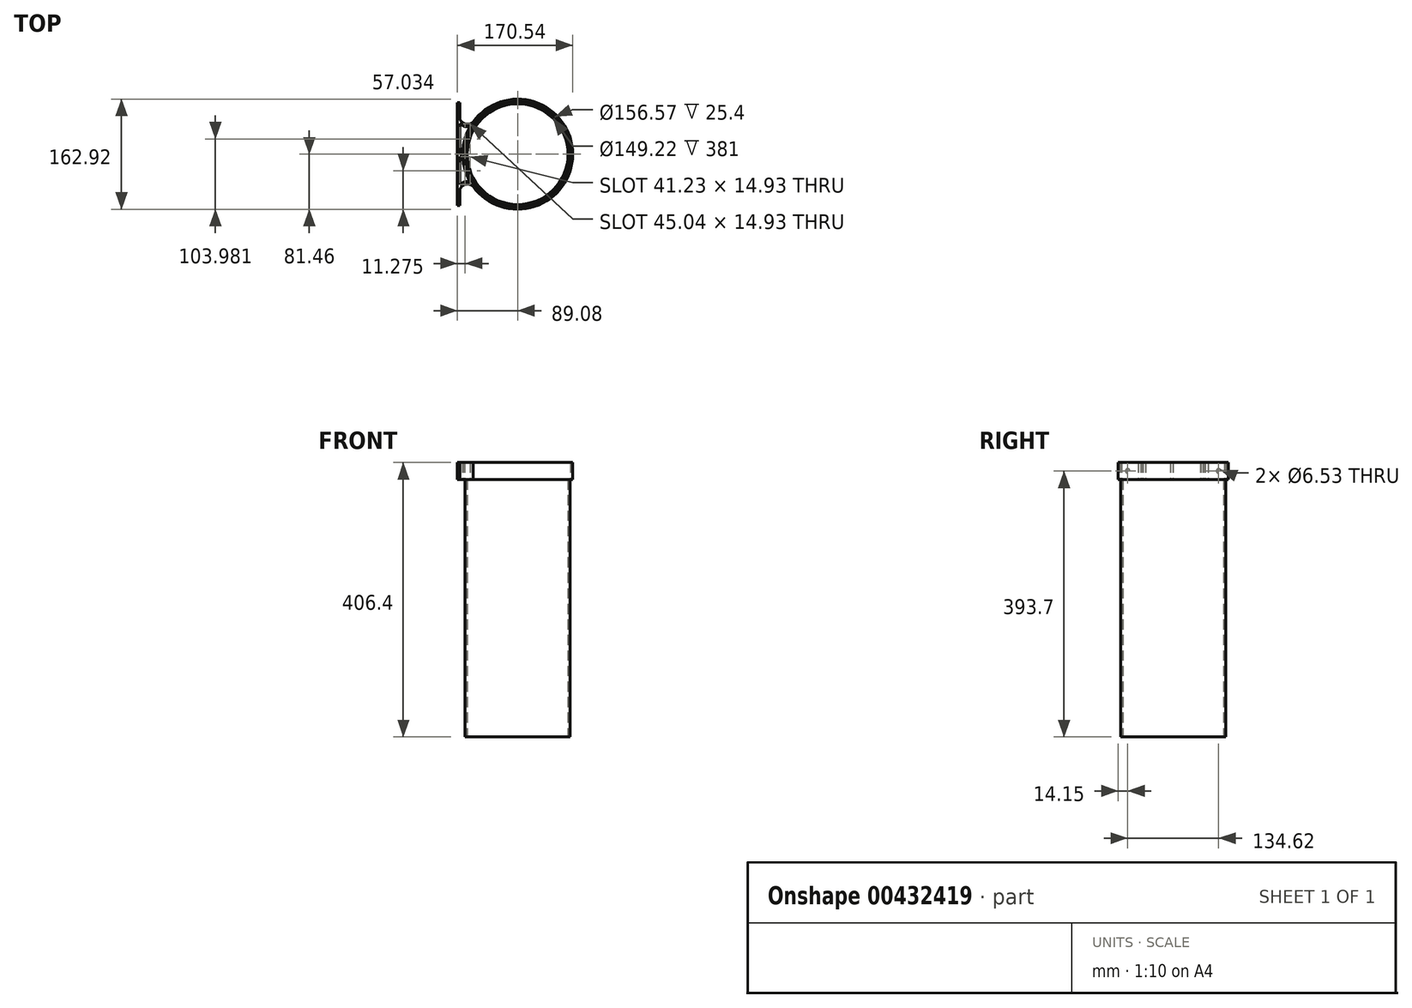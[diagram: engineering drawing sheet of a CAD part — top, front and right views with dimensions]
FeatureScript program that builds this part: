
annotation { "Feature Type Name" : "Feature", "Feature Type Description" : "" }
export const myFeature = defineFeature(function(context is Context, id is Id, definition is map)
    precondition{}
    {
        {
            var Q0;
            Q0=qCreatedBy(makeId("Top.planeOp"),FACE);
            var sketch = newSketch(context, id + "F0", { "sketchPlane" : qUnion([Q0])});
            skCircle(sketch, "E0", {"center": v(0, 0) * mm, "radius": 77.79 * mm});
            skCircle(sketch, "E1.0", {"center": v(0, 0) * mm, "radius": 74.61 * mm});
            skSolve(sketch);
        }
        {
            var Q0;
            Q0 = qSketchRegion(id + "F0", true);
            extrude(context, id + "F1", {"entities" : qUnion([Q0]), "depth" : 381 * mm});
        }
        {
            var Q0;
            Q0=makeQuery(id+"F1.opExtrude","CAP_FACE",FACE,{"disambiguationData":[OSD([sQuery(id+"F0.wireOp",EDGE,"E0"),sQuery(id+"F0.wireOp",EDGE,"E1.0")])],"isStart":false});
            var sketch = newSketch(context, id + "F2", { "sketchPlane" : qUnion([Q0])});
            skCircle(sketch, "E2", {"center": v(0, 0) * mm, "radius": 78.29 * mm});
            skLineSegment(sketch, "E3", {"start": v(77.79, 0) * mm, "end": v(78.29, 0) * mm});
            skArc(sketch, "E4.0", {"start": v(-70.34, 41.1) * mm, "mid": v(68.26, -44.46) * mm, "end": v(-66.02, 47.72) * mm});
            skLineSegment(sketch, "E5", {"start": v(-81.46, 0) * mm, "end": v(-89.08, 0) * mm});
            skLineSegment(sketch, "E6", {"start": v(-89.08, 0) * mm, "end": v(-89.08, 76.2) * mm});
            skLineSegment(sketch, "E7.0", {"start": v(-85.27, 0) * mm, "end": v(-85.27, 45.04) * mm});
            skArc(sketch, "E8", {"start": v(-85.27, 51.62) * mm, "mid": v(-76.67, 44.64) * mm, "end": v(-66.02, 47.72) * mm});
            skArc(sketch, "E9.0", {"start": v(-85.27, 45.04) * mm, "mid": v(-78.32, 41.11) * mm, "end": v(-70.34, 41.1) * mm});
            skLineSegment(sketch, "E10.trimOffspring", {"start": v(-85.27, 51.62) * mm, "end": v(-85.27, 76.2) * mm});
            skLineSegment(sketch, "E11", {"start": v(-89.08, 76.2) * mm, "end": v(-85.27, 76.2) * mm});
            skLineSegment(sketch, "E12.MirrorCS", {"start": v(-89.08, -76.2) * mm, "end": v(-85.27, -76.2) * mm});
            skArc(sketch, "E13.MirrorCS", {"start": v(-85.27, -51.62) * mm, "mid": v(-76.67, -44.64) * mm, "end": v(-66.02, -47.72) * mm});
            skLineSegment(sketch, "E14.MirrorCS", {"start": v(-85.27, 0) * mm, "end": v(-85.27, -45.04) * mm});
            skLineSegment(sketch, "E15.MirrorCS", {"start": v(-89.08, 0) * mm, "end": v(-89.08, -76.2) * mm});
            skArc(sketch, "E16.MirrorCS", {"start": v(-85.27, -45.04) * mm, "mid": v(-78.32, -41.11) * mm, "end": v(-70.34, -41.1) * mm});
            skLineSegment(sketch, "E17.MirrorCS", {"start": v(-85.27, -51.62) * mm, "end": v(-85.27, -76.2) * mm});
            skLineSegment(sketch, "E18", {"start": v(-85.27, 0) * mm, "end": v(-85.27, 3.81) * mm});
            skLineSegment(sketch, "E19", {"start": v(-85.27, 3.81) * mm, "end": v(-81.37, 3.81) * mm});
            skLineSegment(sketch, "E20.MirrorCS", {"start": v(-85.27, -3.81) * mm, "end": v(-81.37, -3.81) * mm});
            skSolve(sketch);
        }
        {
            var Q0;
            Q0 = qSketchRegion(id + "F2", true);
            var Q1;
            {var subQ4=sQuery(id+"F2.wireOp",EDGE,"E18");Q1=makeQuery(id+"F2.imprint","IMPRINT",FACE,{"disambiguationData":[TD([[makeQuery(id+"F2.imprint","IMPRINT",EDGE,{"derivedFrom":subQ4}),-1.0]])]});}
            var Q2;
            {var subQ3=sQuery(id+"F2.wireOp",EDGE,"E20.MirrorCS");Q2=makeQuery(id+"F2.imprint","IMPRINT",FACE,{"disambiguationData":[TD([[makeQuery(id+"F2.imprint","IMPRINT",EDGE,{"derivedFrom":subQ3}),1.0]])]});}
            extrude(context, id + "F3", {"entities" : qUnion([Q0, Q1, Q2]), "depth" : 25.4 * mm});
        }
        {
            var Q0;
            Q0=makeQuery(id+"F3.opExtrude","SWEPT_FACE",FACE,{"disambiguationData":[OSD([sQuery(id+"F2.wireOp",EDGE,"E10.trimOffspring")])]});
            var sketch = newSketch(context, id + "F4", { "sketchPlane" : qUnion([Q0])});
            skLineSegment(sketch, "E21", {"start": v(0, 0) * mm, "end": v(0, -127) * mm});
            skLineSegment(sketch, "E22", {"start": v(76.2, 393.7) * mm, "end": v(67.31, 393.7) * mm});
            skPoint(sketch, "E22.endSnap0", {"position": v(76.2, 393.7) * mm});
            skPoint(sketch, "E23.MirrorP", {"position": v(-76.2, 393.7) * mm});
            skLineSegment(sketch, "E24.MirrorCS", {"start": v(-76.2, 393.7) * mm, "end": v(-67.31, 393.7) * mm});
            skSolve(sketch);
        }
        {
            var Q0;
            Q0=sQuery(id+"F4.wireOp",VERTEX,"E22.end");
            var Q1;
            Q1=sQuery(id+"F4.wireOp",VERTEX,"E24.MirrorCS.end");
            var Q2;
            Q2=makeQuery(id+"F3.opExtrude","SWEPT_BODY",BODY,{"disambiguationData":[OSD([sQuery(id+"F2.wireOp",EDGE,"E2"),sQuery(id+"F2.wireOp",EDGE,"E4.0"),sQuery(id+"F2.wireOp",EDGE,"E6"),sQuery(id+"F2.wireOp",EDGE,"E7.0"),sQuery(id+"F2.wireOp",EDGE,"E8"),sQuery(id+"F2.wireOp",EDGE,"E9.0"),sQuery(id+"F2.wireOp",EDGE,"E10.trimOffspring"),sQuery(id+"F2.wireOp",EDGE,"E11"),sQuery(id+"F2.wireOp",EDGE,"E12.MirrorCS"),sQuery(id+"F2.wireOp",EDGE,"E13.MirrorCS"),sQuery(id+"F2.wireOp",EDGE,"E14.MirrorCS"),sQuery(id+"F2.wireOp",EDGE,"E15.MirrorCS"),sQuery(id+"F2.wireOp",EDGE,"E16.MirrorCS"),sQuery(id+"F2.wireOp",EDGE,"E17.MirrorCS"),sQuery(id+"F2.wireOp",EDGE,"E18")])]});
            hole(context, id + "F5", {"style" : HoleStyle.SIMPLE, "endStyle" : HoleEndStyle.BLIND, "standardTappedOrClearance" : lookupTablePath({ "standard" : "ANSI", "fit" : "Close", "size" : "1/4", "type" : "Clearance" }), "standardBlindInLast" : lookupTablePath({ "fit" : "Close", "standard" : "ANSI", "size" : "1/4", "type" : "Clearance" }), "holeDiameter" : 6.53 * mm, "holeDepth" : 12.7 * mm, "isTappedThrough" : true, "tappedDepth" : 10.8 * mm, "tapClearance" : 3, "locations" : qUnion([Q0, Q1]), "scope" : qUnion([Q2])});
        }
    });
